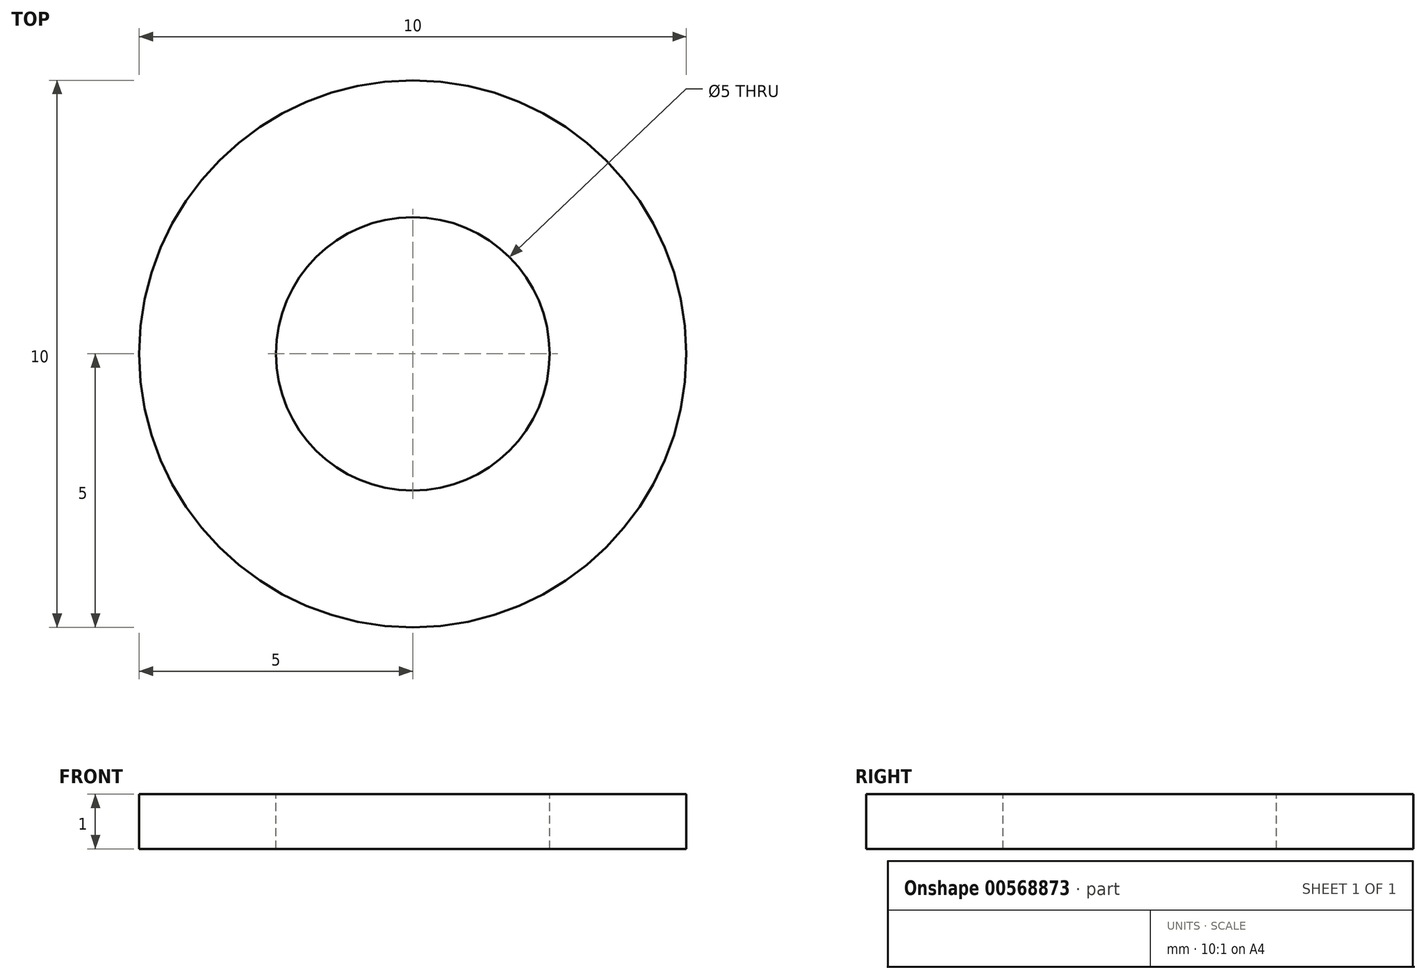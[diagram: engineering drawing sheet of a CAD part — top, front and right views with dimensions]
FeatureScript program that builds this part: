
annotation { "Feature Type Name" : "Feature", "Feature Type Description" : "" }
export const myFeature = defineFeature(function(context is Context, id is Id, definition is map)
    precondition{}
    {
        {
            var Q0;
            Q0=qCreatedBy(makeId("Front.planeOp"),FACE);
            var sketch = newSketch(context, id + "F0", { "sketchPlane" : qUnion([Q0])});
            skLineSegment(sketch, "E0.bottom", {"start": v(-5, 1) * mm, "end": v(-2.5, 1) * mm});
            skLineSegment(sketch, "E0.top", {"start": v(-5, 0) * mm, "end": v(-2.5, 0) * mm});
            skLineSegment(sketch, "E0.left", {"start": v(-5, 1) * mm, "end": v(-5, 0) * mm});
            skLineSegment(sketch, "E0.right", {"start": v(-2.5, 1) * mm, "end": v(-2.5, 0) * mm});
            skLineSegment(sketch, "E1", {"start": v(0, 14.04) * mm, "end": v(0, -14.67) * mm, "construction": true});
            skSolve(sketch);
        }
        {
            var Q0;
            Q0 = qSketchRegion(id + "F0", true);
            var Q1;
            Q1=sQuery(id+"F0.wireOp",EDGE,"E1");
            revolve(context, id + "F1", {"entities" : qUnion([Q0]), "axis" : qUnion([Q1]), "revolveType" : RevolveType.FULL});
        }
    });
